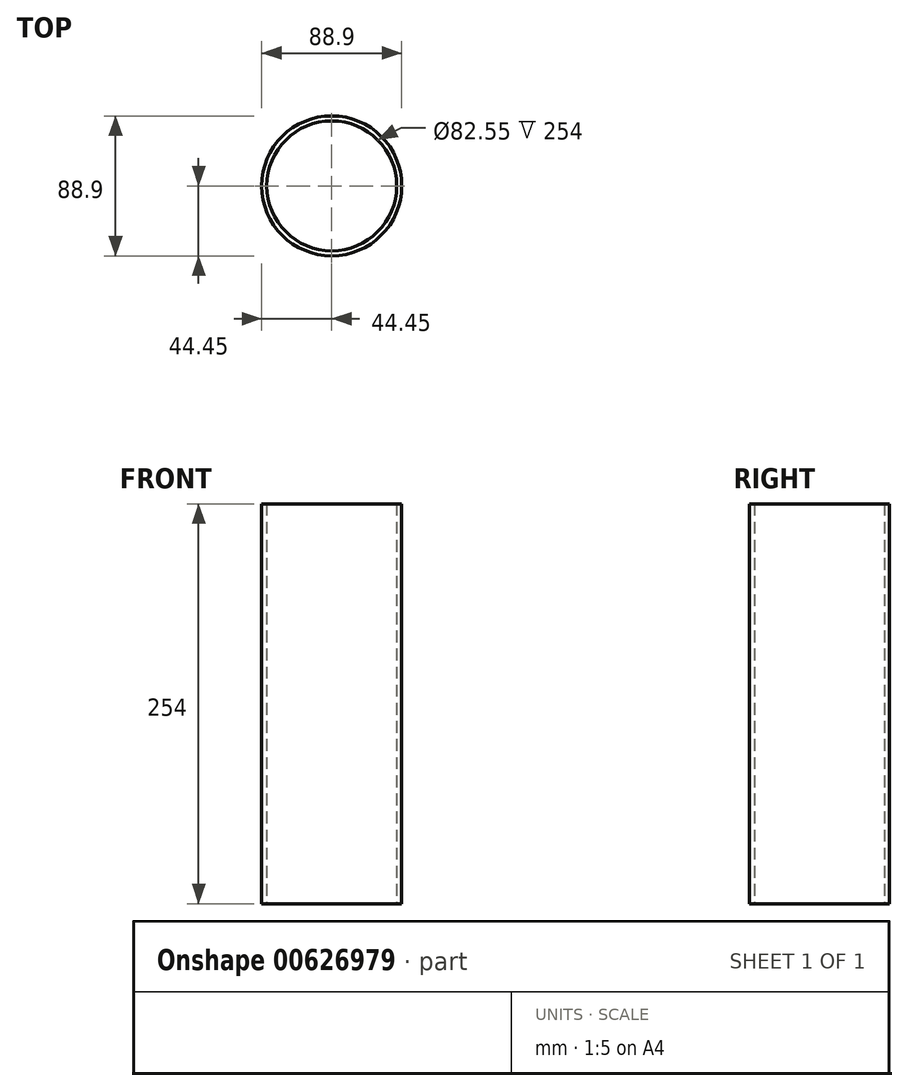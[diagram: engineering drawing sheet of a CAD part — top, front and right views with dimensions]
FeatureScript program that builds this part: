
annotation { "Feature Type Name" : "Feature", "Feature Type Description" : "" }
export const myFeature = defineFeature(function(context is Context, id is Id, definition is map)
    precondition{}
    {
        {
            var Q0;
            Q0=qCreatedBy(makeId("Top.planeOp"),FACE);
            var sketch = newSketch(context, id + "F0", { "sketchPlane" : qUnion([Q0])});
            skCircle(sketch, "E0", {"center": v(0, 0) * mm, "radius": 41.28 * mm});
            skCircle(sketch, "E1", {"center": v(0, 0) * mm, "radius": 44.45 * mm});
            skSolve(sketch);
        }
        {
            var Q0;
            Q0 = qSketchRegion(id + "F0", true);
            extrude(context, id + "F1", {"entities" : qUnion([Q0]), "depth" : 254 * mm, "offsetDistance" : 25.4 * mm, "symmetric" : true});
        }
    });
